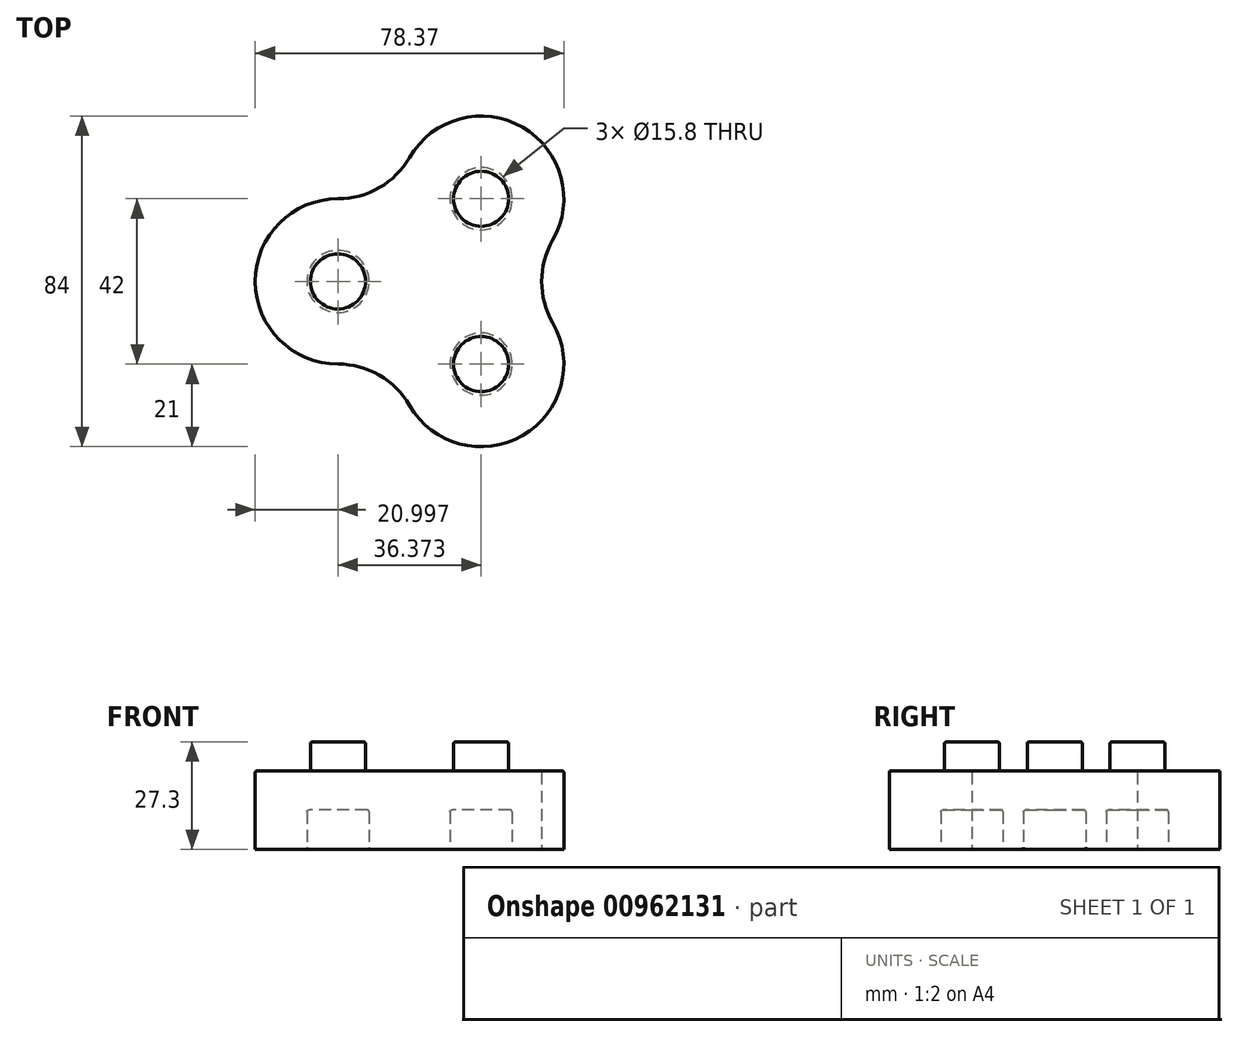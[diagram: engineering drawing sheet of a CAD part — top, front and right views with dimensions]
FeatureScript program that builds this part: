
annotation { "Feature Type Name" : "Feature", "Feature Type Description" : "" }
export const myFeature = defineFeature(function(context is Context, id is Id, definition is map)
    precondition{}
    {
        {
            assignVariable(context, id + "F0", {"name" : "inner_circle_extrude", "anyValue" : 10});
        }
        {
            assignVariable(context, id + "F1", {"name" : "nipple_circle_extrude", "anyValue" : 7.3});
        }
        {
            assignVariable(context, id + "F2", {"name" : "outer_circle_extrude", "anyValue" : 20});
        }
        {
            assignVariable(context, id + "F3", {"name" : "fillet", "anyValue" : 0.5});
        }
        {
            var Q0;
            Q0=qCreatedBy(makeId("Top.planeOp"),FACE);
            var sketch = newSketch(context, id + "F4", { "sketchPlane" : qUnion([Q0])});
            skCircle(sketch, "E0", {"center": v(0, 42) * mm, "radius": 7.9 * mm});
            skCircle(sketch, "E1", {"center": v(0, 0) * mm, "radius": 7.9 * mm});
            skArc(sketch, "E2.converted", {"start": v(18.19, 31.5) * mm, "mid": v(10.5, 60.19) * mm, "end": v(-18.19, 52.5) * mm});
            skArc(sketch, "E3.converted", {"start": v(-18.19, 10.5) * mm, "mid": v(-18.54, 9.87) * mm, "end": v(-18.87, 9.22) * mm});
            skPoint(sketch, "E4.orphan", {"position": v(-18.87, 9.22) * mm});
            skArc(sketch, "E5.MirrorC", {"start": v(18.19, 10.5) * mm, "mid": v(15.37, 21) * mm, "end": v(18.19, 31.5) * mm});
            skArc(sketch, "E6.converted", {"start": v(-36.37, 42) * mm, "mid": v(-57.37, 21) * mm, "end": v(-36.37, 0) * mm});
            skArc(sketch, "E7", {"start": v(-36.37, 42) * mm, "mid": v(-25.87, 44.81) * mm, "end": v(-18.19, 52.5) * mm});
            skArc(sketch, "E8", {"start": v(-18.19, -10.5) * mm, "mid": v(-25.87, -2.81) * mm, "end": v(-36.37, 0) * mm});
            skArc(sketch, "E9.trimOffspring", {"start": v(-18.19, -10.5) * mm, "mid": v(10.5, -18.19) * mm, "end": v(18.19, 10.5) * mm});
            skCircle(sketch, "E10", {"center": v(-36.37, 21) * mm, "radius": 7.9 * mm});
            skSolve(sketch);
        }
        {
            var Q0;
            Q0=makeQuery(id+"F4.imprint","IMPRINT",FACE,{"disambiguationData":[TD([[makeQuery(id+"F4.imprint","IMPRINT",EDGE,{"derivedFrom":sQuery(id+"F4.wireOp",EDGE,"ScaTM9CG-l0WX-AUfX-dH3G-diZ5i2Zft3Bz")}),1.0]])]});
            var Q1;
            Q1=makeQuery(id+"F4.imprint","IMPRINT",FACE,{"disambiguationData":[TD([[makeQuery(id+"F4.imprint","IMPRINT",EDGE,{"derivedFrom":sQuery(id+"F4.wireOp",EDGE,"E0")}),1.0]])]});
            var Q2;
            Q2=makeQuery(id+"F4.imprint","IMPRINT",FACE,{"disambiguationData":[TD([[makeQuery(id+"F4.imprint","IMPRINT",EDGE,{"derivedFrom":sQuery(id+"F4.wireOp",EDGE,"E1")}),1.0]])]});
            var Q3;
            Q3=makeQuery(id+"F4.imprint","IMPRINT",FACE,{"disambiguationData":[TD([[makeQuery(id+"F4.imprint","IMPRINT",EDGE,{"derivedFrom":sQuery(id+"F4.wireOp",EDGE,"E0")}),-1.0]])]});
            var Q4;
            Q4=makeQuery(id+"F4.imprint","IMPRINT",FACE,{"disambiguationData":[TD([[makeQuery(id+"F4.imprint","IMPRINT",EDGE,{"derivedFrom":sQuery(id+"F4.wireOp",EDGE,"E10")}),1.0]])]});
            extrude(context, id + "F5", {"entities" : qUnion([Q0, Q1, Q2, Q3, Q4]), "depth" : (getVariable(context, 'outer_circle_extrude')) * mm, "offsetDistance" : 25 * mm});
        }
        {
            var Q0;
            Q0=makeQuery(id+"F4.imprint","IMPRINT",FACE,{"disambiguationData":[TD([[makeQuery(id+"F4.imprint","IMPRINT",EDGE,{"derivedFrom":sQuery(id+"F4.wireOp",EDGE,"E0")}),1.0]])]});
            var Q1;
            Q1=makeQuery(id+"F4.imprint","IMPRINT",FACE,{"disambiguationData":[TD([[makeQuery(id+"F4.imprint","IMPRINT",EDGE,{"derivedFrom":sQuery(id+"F4.wireOp",EDGE,"E1")}),1.0]])]});
            var Q2;
            Q2=makeQuery(id+"F4.imprint","IMPRINT",FACE,{"disambiguationData":[TD([[makeQuery(id+"F4.imprint","IMPRINT",EDGE,{"derivedFrom":sQuery(id+"F4.wireOp",EDGE,"E10")}),1.0]])]});
            extrude(context, id + "F6", {"entities" : qUnion([Q0, Q1, Q2]), "operationType" : NewBodyOperationType.REMOVE, "depth" : (getVariable(context, 'inner_circle_extrude')) * mm, "offsetDistance" : 25 * mm});
        }
        {
            var Q0;
            Q0=makeQuery(id+"F5.opExtrude","CAP_FACE",FACE,{"disambiguationData":[OSD([sQuery(id+"F4.wireOp",EDGE,"E2.converted"),sQuery(id+"F4.wireOp",EDGE,"E3.converted"),sQuery(id+"F4.wireOp",EDGE,"MIaug4t6-5uLj-SX17-JixO-nkbqJCue0yvX"),sQuery(id+"F4.wireOp",EDGE,"E5.MirrorC")])],"isStart":false});
            var sketch = newSketch(context, id + "F7", { "sketchPlane" : qUnion([Q0])});
            skCircle(sketch, "E11", {"center": v(0, 0) * mm, "radius": 7 * mm});
            skCircle(sketch, "E12", {"center": v(0, 42) * mm, "radius": 7 * mm});
            skCircle(sketch, "E13", {"center": v(-36.37, 21) * mm, "radius": 7 * mm});
            skSolve(sketch);
        }
        {
            var Q0;
            Q0=makeQuery(id+"F7.imprint","IMPRINT",FACE,{"disambiguationData":[TD([[makeQuery(id+"F7.imprint","IMPRINT",EDGE,{"derivedFrom":sQuery(id+"F7.wireOp",EDGE,"E11")}),1.0]])]});
            var Q1;
            Q1=makeQuery(id+"F7.imprint","IMPRINT",FACE,{"disambiguationData":[TD([[makeQuery(id+"F7.imprint","IMPRINT",EDGE,{"derivedFrom":sQuery(id+"F7.wireOp",EDGE,"Dg55u7MG-Wcnn-qXMQ-j3jR-78wnB7IFwmOc")}),1.0]])]});
            var Q2;
            Q2=makeQuery(id+"F7.imprint","IMPRINT",FACE,{"disambiguationData":[TD([[makeQuery(id+"F7.imprint","IMPRINT",EDGE,{"derivedFrom":sQuery(id+"F7.wireOp",EDGE,"E12")}),1.0]])]});
            var Q3;
            Q3=makeQuery(id+"F7.imprint","IMPRINT",FACE,{"disambiguationData":[TD([[makeQuery(id+"F7.imprint","IMPRINT",EDGE,{"derivedFrom":sQuery(id+"F7.wireOp",EDGE,"E13")}),1.0]])]});
            extrude(context, id + "F8", {"entities" : qUnion([Q0, Q1, Q2, Q3]), "operationType" : NewBodyOperationType.ADD, "depth" : (getVariable(context, 'nipple_circle_extrude')) * mm, "offsetDistance" : 25 * mm});
        }
        {
            var Q0;
            Q0=makeQuery(id+"F8.opExtrude","CAP_EDGE",EDGE,{"disambiguationData":[OSD([sQuery(id+"F7.wireOp",EDGE,"E11")])],"isStart":false});
            var Q1;
            Q1=makeQuery(id+"F5.opExtrude","CAP_EDGE",EDGE,{"disambiguationData":[OSD([sQuery(id+"F4.wireOp",EDGE,"ScaTM9CG-l0WX-AUfX-dH3G-diZ5i2Zft3Bz")])],"isStart":false});
            var Q2;
            Q2=makeQuery(id+"F5.opExtrude","CAP_EDGE",EDGE,{"disambiguationData":[OSD([sQuery(id+"F4.wireOp",EDGE,"ScaTM9CG-l0WX-AUfX-dH3G-diZ5i2Zft3Bz")])],"isStart":true});
            var Q3;
            Q3=makeQuery(id+"F6.boolean.opBoolean","COPY",EDGE,{"derivedFrom":makeQuery(id+"F6.opExtrude","CAP_EDGE",EDGE,{"disambiguationData":[OSD([sQuery(id+"F4.wireOp",EDGE,"E0")])],"isStart":true})});
            var Q4;
            Q4=makeQuery(id+"F6.boolean.opBoolean","COPY",FACE,{"derivedFrom":makeQuery(id+"F6.opExtrude","CAP_FACE",FACE,{"disambiguationData":[OSD([sQuery(id+"F4.wireOp",EDGE,"E0")])],"isStart":false})});
            var Q5;
            Q5=makeQuery(id+"F6.boolean.opBoolean","COPY",EDGE,{"derivedFrom":makeQuery(id+"F6.opExtrude","CAP_EDGE",EDGE,{"disambiguationData":[OSD([sQuery(id+"F4.wireOp",EDGE,"E1")])],"isStart":true})});
            var Q6;
            Q6=makeQuery(id+"F6.boolean.opBoolean","COPY",EDGE,{"derivedFrom":makeQuery(id+"F6.opExtrude","CAP_EDGE",EDGE,{"disambiguationData":[OSD([sQuery(id+"F4.wireOp",EDGE,"E1")])],"isStart":false})});
            var Q7;
            Q7=makeQuery(id+"F8.opExtrude","CAP_EDGE",EDGE,{"disambiguationData":[OSD([sQuery(id+"F7.wireOp",EDGE,"Dg55u7MG-Wcnn-qXMQ-j3jR-78wnB7IFwmOc")])],"isStart":true});
            var Q8;
            Q8=makeQuery(id+"F8.opExtrude","CAP_EDGE",EDGE,{"disambiguationData":[OSD([sQuery(id+"F7.wireOp",EDGE,"Dg55u7MG-Wcnn-qXMQ-j3jR-78wnB7IFwmOc")])],"isStart":false});
            var Q9;
            Q9=makeQuery(id+"F8.opExtrude","CAP_EDGE",EDGE,{"disambiguationData":[OSD([sQuery(id+"F7.wireOp",EDGE,"E12")])],"isStart":false});
            var Q10;
            Q10=makeQuery(id+"F8.opExtrude","CAP_EDGE",EDGE,{"disambiguationData":[OSD([sQuery(id+"F7.wireOp",EDGE,"E12")])],"isStart":true});
            var Q11;
            Q11=makeQuery(id+"F5.opExtrude","CAP_EDGE",EDGE,{"disambiguationData":[OSD([sQuery(id+"F4.wireOp",EDGE,"E2.converted")])],"isStart":false});
            var Q12;
            Q12=makeQuery(id+"F8.opExtrude","CAP_EDGE",EDGE,{"disambiguationData":[OSD([sQuery(id+"F7.wireOp",EDGE,"E13")])],"isStart":true});
            var Q13;
            Q13=makeQuery(id+"F8.opExtrude","CAP_EDGE",EDGE,{"disambiguationData":[OSD([sQuery(id+"F7.wireOp",EDGE,"E13")])],"isStart":false});
            var Q14;
            Q14=makeQuery(id+"F6.boolean.opBoolean","COPY",FACE,{"derivedFrom":makeQuery(id+"F6.opExtrude","SWEPT_FACE",FACE,{"disambiguationData":[OSD([sQuery(id+"F4.wireOp",EDGE,"E10")])]})});
            var Q15;
            Q15=makeQuery(id+"F8.opExtrude","CAP_EDGE",EDGE,{"disambiguationData":[OSD([sQuery(id+"F7.wireOp",EDGE,"E11")])],"isStart":true});
            fillet(context, id + "F9", {"entities" : qUnion([Q0, Q1, Q2, Q3, Q4, Q5, Q6, Q7, Q8, Q9, Q10, Q11, Q12, Q13, Q14, Q15]), "radius" : (getVariable(context, 'fillet')) * mm, "tangentPropagation" : true, "allowEdgeOverflow" : false});
        }
    });
